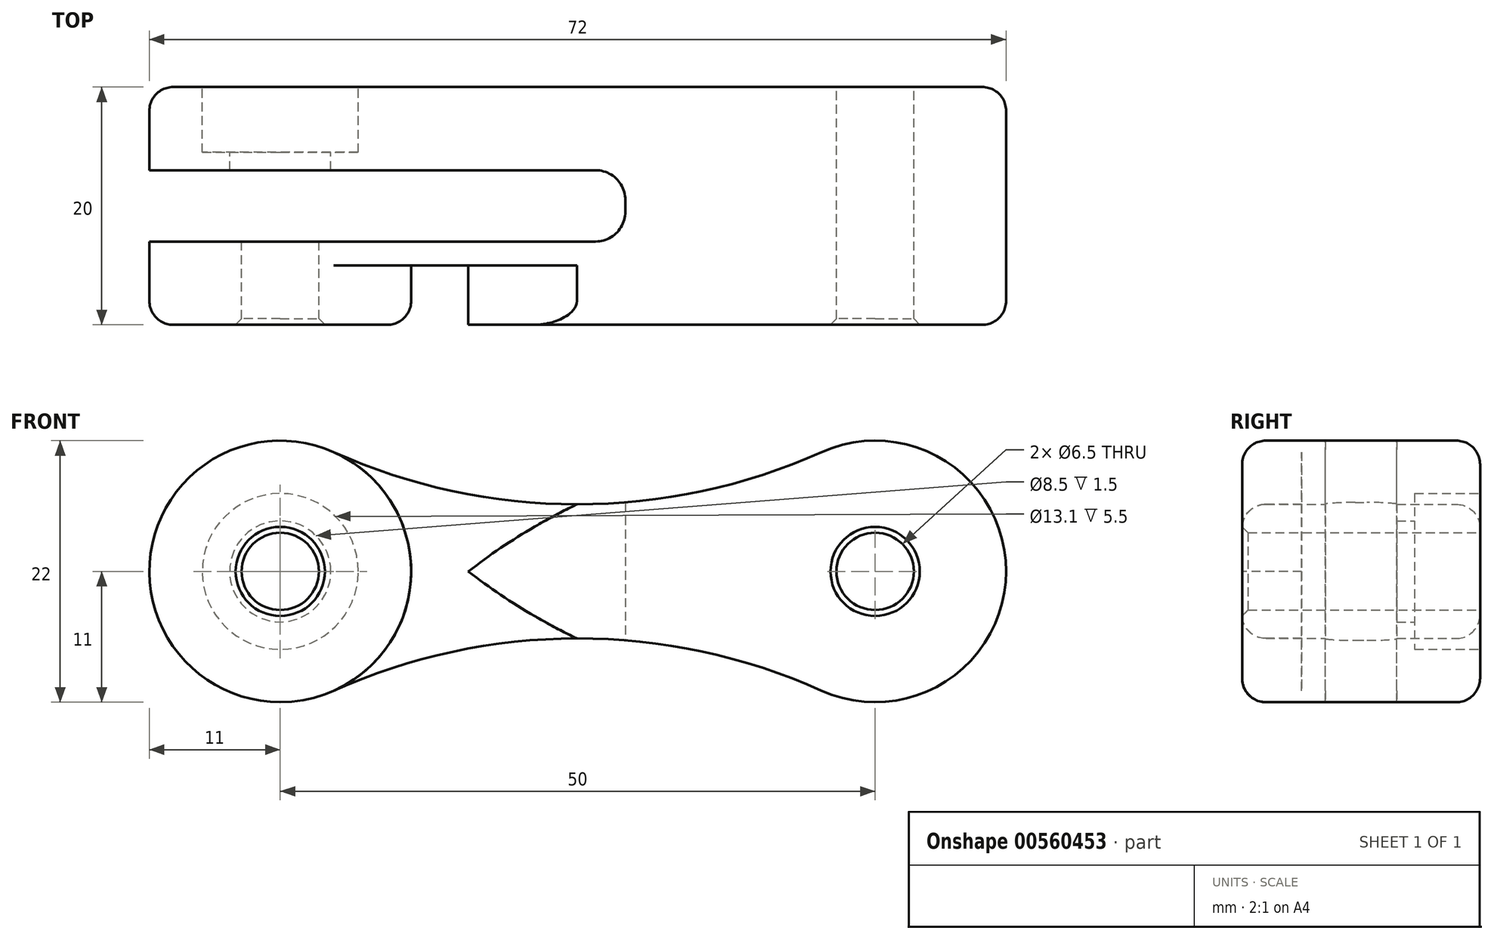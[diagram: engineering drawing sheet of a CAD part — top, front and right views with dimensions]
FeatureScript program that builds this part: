
annotation { "Feature Type Name" : "Feature", "Feature Type Description" : "" }
export const myFeature = defineFeature(function(context is Context, id is Id, definition is map)
    precondition{}
    {
        {
            var Q0;
            Q0=qCreatedBy(makeId("Front.planeOp"),FACE);
            var sketch = newSketch(context, id + "F0", { "sketchPlane" : qUnion([Q0])});
            skArc(sketch, "E0", {"start": v(-20.5, 10.03) * mm, "mid": v(-36, 0) * mm, "end": v(-20.5, -10.03) * mm});
            skArc(sketch, "E1", {"start": v(20.5, -10.03) * mm, "mid": v(36, 0) * mm, "end": v(20.5, 10.03) * mm});
            skArc(sketch, "E2", {"start": v(-20.5, 10.03) * mm, "mid": v(0, 5.64) * mm, "end": v(20.5, 10.03) * mm});
            skLineSegment(sketch, "E3", {"start": v(-25, 0) * mm, "end": v(25, 0) * mm, "construction": true});
            skArc(sketch, "E4.MirrorC", {"start": v(-20.5, -10.03) * mm, "mid": v(0, -5.64) * mm, "end": v(20.5, -10.03) * mm});
            skSolve(sketch);
        }
        {
            var Q0;
            Q0=makeQuery(id+"F0.imprint","IMPRINT",FACE,{"disambiguationData":[TD([[makeQuery(id+"F0.imprint","IMPRINT",EDGE,{"derivedFrom":sQuery(id+"F0.wireOp",EDGE,"E0")}),1.0]])]});
            extrude(context, id + "F1", {"entities" : qUnion([Q0]), "endBound" : BoundingType.SYMMETRIC, "depth" : 20 * mm, "offsetDistance" : 25 * mm});
        }
        {
            var Q0;
            Q0=makeQuery(id+"F1.opExtrude","CAP_FACE",FACE,{"disambiguationData":[OSD([sQuery(id+"F0.wireOp",EDGE,"E0"),sQuery(id+"F0.wireOp",EDGE,"E1"),sQuery(id+"F0.wireOp",EDGE,"E2"),sQuery(id+"F0.wireOp",EDGE,"E4.MirrorC")])],"isStart":true});
            var sketch = newSketch(context, id + "F2", { "sketchPlane" : qUnion([Q0])});
            skCircle(sketch, "E5", {"center": v(25, 0) * mm, "radius": 4.25 * mm});
            skCircle(sketch, "E6", {"center": v(-25, 0) * mm, "radius": 4.25 * mm});
            skSolve(sketch);
        }
        {
            var Q0;
            Q0=makeQuery(id+"F2.imprint","IMPRINT",FACE,{"disambiguationData":[TD([[makeQuery(id+"F2.imprint","IMPRINT",EDGE,{"derivedFrom":sQuery(id+"F2.wireOp",EDGE,"E5")}),-1.0]])]});
            var sketch = newSketch(context, id + "F3", { "sketchPlane" : qUnion([Q0])});
            skCircle(sketch, "E7", {"center": v(-25, 0) * mm, "radius": 3.25 * mm});
            skCircle(sketch, "E8", {"center": v(25, 0) * mm, "radius": 3.25 * mm});
            skSolve(sketch);
        }
        {
            var Q0;
            Q0=makeQuery(id+"F3.imprint","IMPRINT",FACE,{"disambiguationData":[TD([[makeQuery(id+"F3.imprint","IMPRINT",EDGE,{"derivedFrom":sQuery(id+"F3.wireOp",EDGE,"E7")}),1.0]])]});
            var Q1;
            Q1=makeQuery(id+"F3.imprint","IMPRINT",FACE,{"disambiguationData":[TD([[makeQuery(id+"F3.imprint","IMPRINT",EDGE,{"derivedFrom":sQuery(id+"F3.wireOp",EDGE,"E8")}),1.0]])]});
            extrude(context, id + "F4", {"entities" : qUnion([Q0, Q1]), "operationType" : NewBodyOperationType.REMOVE, "endBound" : BoundingType.THROUGH_ALL, "oppositeDirection" : true, "depth" : 25 * mm, "offsetDistance" : 25 * mm});
        }
        {
            var Q0;
            Q0=makeQuery(id+"F2.imprint","IMPRINT",FACE,{"disambiguationData":[TD([[makeQuery(id+"F2.imprint","IMPRINT",EDGE,{"derivedFrom":sQuery(id+"F2.wireOp",EDGE,"E5")}),1.0]])]});
            extrude(context, id + "F5", {"entities" : qUnion([Q0]), "operationType" : NewBodyOperationType.REMOVE, "oppositeDirection" : true, "depth" : 9 * mm, "offsetDistance" : 25 * mm});
        }
        {
            var Q0;
            Q0=makeQuery(id+"F1.opExtrude","CAP_FACE",FACE,{"disambiguationData":[OSD([sQuery(id+"F0.wireOp",EDGE,"E0"),sQuery(id+"F0.wireOp",EDGE,"E1"),sQuery(id+"F0.wireOp",EDGE,"E2"),sQuery(id+"F0.wireOp",EDGE,"E4.MirrorC")])],"isStart":true});
            var sketch = newSketch(context, id + "F6", { "sketchPlane" : qUnion([Q0])});
            skCircle(sketch, "E9", {"center": v(25, 0) * mm, "radius": 6.55 * mm});
            skSolve(sketch);
        }
        {
            var Q0;
            Q0=makeQuery(id+"F6.imprint","IMPRINT",FACE,{"disambiguationData":[TD([[makeQuery(id+"F6.imprint","IMPRINT",EDGE,{"derivedFrom":sQuery(id+"F6.wireOp",EDGE,"E9")}),1.0]])]});
            extrude(context, id + "F7", {"entities" : qUnion([Q0]), "operationType" : NewBodyOperationType.REMOVE, "oppositeDirection" : true, "depth" : 5.5 * mm, "offsetDistance" : 25 * mm});
        }
        {
            var Q0;
            Q0=makeQuery(id+"F1.opExtrude","CAP_FACE",FACE,{"disambiguationData":[OSD([sQuery(id+"F0.wireOp",EDGE,"E0"),sQuery(id+"F0.wireOp",EDGE,"E1"),sQuery(id+"F0.wireOp",EDGE,"E2"),sQuery(id+"F0.wireOp",EDGE,"E4.MirrorC")])],"isStart":false});
            var sketch = newSketch(context, id + "F8", { "sketchPlane" : qUnion([Q0])});
            skArc(sketch, "E10", {"start": v(-9.19, 0) * mm, "mid": v(-2.1, -4.6) * mm, "end": v(5.65, -7.96) * mm});
            skLineSegment(sketch, "E11", {"start": v(-45.02, 0) * mm, "end": v(-102.32, 0) * mm, "construction": true});
            skArc(sketch, "E12.MirrorC", {"start": v(-9.19, 0) * mm, "mid": v(-2.1, 4.6) * mm, "end": v(5.65, 7.96) * mm});
            skLineSegment(sketch, "E13", {"start": v(5.65, -7.96) * mm, "end": v(-41.27, -16.1) * mm});
            skLineSegment(sketch, "E14", {"start": v(-41.27, -16.1) * mm, "end": v(-41.27, 0) * mm});
            skLineSegment(sketch, "E15.MirrorCS", {"start": v(-41.27, 16.1) * mm, "end": v(-41.27, 0) * mm});
            skLineSegment(sketch, "E16.MirrorCS", {"start": v(5.65, 7.96) * mm, "end": v(-41.27, 16.1) * mm});
            skCircle(sketch, "E17", {"center": v(-25, 0) * mm, "radius": 11 * mm});
            skSolve(sketch);
        }
        {
            var Q0;
            Q0 = qSketchRegion(id + "F8", true);
            extrude(context, id + "F9", {"entities" : qUnion([Q0]), "operationType" : NewBodyOperationType.REMOVE, "oppositeDirection" : true, "depth" : 5 * mm, "offsetDistance" : 25 * mm});
        }
        {
            var Q0;
            Q0=makeQuery(id+"F1.opExtrude","CAP_FACE",FACE,{"disambiguationData":[OSD([sQuery(id+"F0.wireOp",EDGE,"E0"),sQuery(id+"F0.wireOp",EDGE,"E1"),sQuery(id+"F0.wireOp",EDGE,"E2"),sQuery(id+"F0.wireOp",EDGE,"E4.MirrorC")])],"isStart":true});
            var sketch = newSketch(context, id + "F10", { "sketchPlane" : qUnion([Q0])});
            skLineSegment(sketch, "E18", {"start": v(-17.42, 0) * mm, "end": v(-74.72, 0) * mm, "construction": true});
            skLineSegment(sketch, "E19", {"start": v(41.27, -16.1) * mm, "end": v(41.27, 0) * mm});
            skLineSegment(sketch, "E20.MirrorCS", {"start": v(41.27, 16.1) * mm, "end": v(41.27, 0) * mm});
            skLineSegment(sketch, "E21.MirrorCS", {"start": v(-5.65, -7.96) * mm, "end": v(41.27, -16.1) * mm});
            skLineSegment(sketch, "E22.MirrorCS", {"start": v(-5.65, 7.96) * mm, "end": v(41.27, 16.1) * mm});
            skArc(sketch, "E23.MirrorCS", {"start": v(9.19, 0) * mm, "mid": v(2.1, -4.6) * mm, "end": v(-5.65, -7.96) * mm});
            skArc(sketch, "E24.MirrorCS", {"start": v(9.19, 0) * mm, "mid": v(2.1, 4.6) * mm, "end": v(-5.65, 7.96) * mm});
            skCircle(sketch, "E25.MirrorC", {"center": v(25, 0) * mm, "radius": 11 * mm});
            skSolve(sketch);
        }
        {
            var Q0;
            Q0=makeQuery(id+"F10.imprint","IMPRINT",FACE,{"disambiguationData":[TD([[makeQuery(id+"F10.imprint","IMPRINT",EDGE,{"derivedFrom":sQuery(id+"F10.wireOp",EDGE,"E19")}),1.0]])]});
            var Q1;
            {var subQ0=sQuery(id+"F10.wireOp",EDGE,"E24.MirrorCS");var subQ1=sQuery(id+"F10.wireOp",EDGE,"E23.MirrorCS");var subQ2=makeQuery(id+"F10.imprint","INTERSECT",VERTEX,{"derivedFrom":[subQ1,subQ0]});Q1=makeQuery(id+"F10.imprint","IMPRINT",FACE,{"disambiguationData":[TD([[makeQuery(id+"F10.imprint","IMPRINT",EDGE,{"disambiguationData":[TD([[subQ2,-1.0]])],"derivedFrom":subQ1}),1.0]])]});}
            extrude(context, id + "F11", {"entities" : qUnion([Q0, Q1]), "operationType" : NewBodyOperationType.REMOVE, "oppositeDirection" : true, "depth" : 5 * mm, "offsetDistance" : 25 * mm});
        }
        {
            var Q0;
            Q0=makeQuery(id+"F9.boolean.opBoolean","MERGE",EDGE,{"derivedFrom":[makeQuery(id+"F1.opExtrude","CAP_EDGE",EDGE,{"disambiguationData":[OSD([sQuery(id+"F0.wireOp",EDGE,"E0")])],"isStart":false}),makeQuery(id+"F9.opExtrude","CAP_EDGE",EDGE,{"disambiguationData":[OSD([sQuery(id+"F8.wireOp",EDGE,"E17")])],"isStart":true})]});
            var Q1;
            Q1=makeQuery(id+"F9.boolean.opBoolean","COPY",EDGE,{"derivedFrom":makeQuery(id+"F9.opExtrude","CAP_EDGE",EDGE,{"disambiguationData":[OSD([sQuery(id+"F8.wireOp",EDGE,"E10")])],"isStart":true})});
            var Q2;
            Q2=makeQuery(id+"F9.boolean.opBoolean","COPY",EDGE,{"derivedFrom":makeQuery(id+"F9.opExtrude","CAP_EDGE",EDGE,{"disambiguationData":[OSD([sQuery(id+"F8.wireOp",EDGE,"E12.MirrorC")])],"isStart":true})});
            var Q3;
            Q3=makeQuery(id+"F1.opExtrude","CAP_EDGE",EDGE,{"disambiguationData":[OSD([sQuery(id+"F0.wireOp",EDGE,"E2")])],"isStart":false});
            var Q4;
            Q4=makeQuery(id+"F1.opExtrude","CAP_EDGE",EDGE,{"disambiguationData":[OSD([sQuery(id+"F0.wireOp",EDGE,"E4.MirrorC")])],"isStart":true});
            var Q5;
            Q5=makeQuery(id+"F11.boolean.opBoolean","COPY",EDGE,{"derivedFrom":makeQuery(id+"F11.opExtrude","CAP_EDGE",EDGE,{"disambiguationData":[OSD([sQuery(id+"F10.wireOp",EDGE,"E23.MirrorCS")])],"isStart":true})});
            var Q6;
            Q6=makeQuery(id+"F11.boolean.opBoolean","COPY",EDGE,{"derivedFrom":makeQuery(id+"F11.opExtrude","CAP_EDGE",EDGE,{"disambiguationData":[OSD([sQuery(id+"F10.wireOp",EDGE,"E24.MirrorCS")])],"isStart":true})});
            var Q7;
            Q7=makeQuery(id+"F11.boolean.opBoolean","MERGE",EDGE,{"derivedFrom":[makeQuery(id+"F1.opExtrude","CAP_EDGE",EDGE,{"disambiguationData":[OSD([sQuery(id+"F0.wireOp",EDGE,"E0")])],"isStart":true}),makeQuery(id+"F11.opExtrude","CAP_EDGE",EDGE,{"disambiguationData":[OSD([sQuery(id+"F10.wireOp",EDGE,"E25.MirrorC")])],"isStart":true})]});
            fillet(context, id + "F12", {"entities" : qUnion([Q0, Q1, Q2, Q3, Q4, Q5, Q6, Q7]), "radius" : 2 * mm, "tangentPropagation" : true, "allowEdgeOverflow" : false});
        }
        {
            var Q0;
            Q0=qCreatedBy(makeId("Right.planeOp"),FACE);
            cPlane(context, id + "F13", {"entities" : qUnion([Q0]), "cplaneType" : CPlaneType.OFFSET, "offset" : 36 * mm, "oppositeDirection" : true, "width" : 150 * mm, "height" : 150 * mm});
        }
        {
            var Q0;
            Q0=qCreatedBy(id+"F13.planeOp",FACE);
            var sketch = newSketch(context, id + "F14", { "sketchPlane" : qUnion([Q0])});
            skLineSegment(sketch, "E26.bottom", {"start": v(-3, 15) * mm, "end": v(3, 15) * mm});
            skLineSegment(sketch, "E26.top", {"start": v(-3, -15) * mm, "end": v(3, -15) * mm});
            skLineSegment(sketch, "E26.left", {"start": v(-3, 15) * mm, "end": v(-3, -15) * mm});
            skLineSegment(sketch, "E26.right", {"start": v(3, 15) * mm, "end": v(3, -15) * mm});
            skPoint(sketch, "E26.middle", {"position": v(0, 0) * mm});
            skSolve(sketch);
        }
        {
            var Q0;
            Q0 = qSketchRegion(id + "F14", true);
            extrude(context, id + "F15", {"entities" : qUnion([Q0]), "operationType" : NewBodyOperationType.REMOVE, "depth" : 40 * mm, "offsetDistance" : 25 * mm});
        }
        {
            var Q0;
            Q0=makeQuery(id+"F15.boolean.opBoolean","COPY",EDGE,{"derivedFrom":makeQuery(id+"F15.opExtrude","CAP_EDGE",EDGE,{"disambiguationData":[OSD([sQuery(id+"F14.wireOp",EDGE,"E26.right")])],"isStart":false})});
            var Q1;
            Q1=makeQuery(id+"F15.boolean.opBoolean","COPY",EDGE,{"derivedFrom":makeQuery(id+"F15.opExtrude","CAP_EDGE",EDGE,{"disambiguationData":[OSD([sQuery(id+"F14.wireOp",EDGE,"E26.left")])],"isStart":false})});
            fillet(context, id + "F16", {"entities" : qUnion([Q0, Q1]), "radius" : 2.5 * mm, "tangentPropagation" : true, "allowEdgeOverflow" : false});
        }
        {
            var Q0;
            Q0=makeQuery(id+"F4.boolean.opBoolean","INTERSECT",EDGE,{"derivedFrom":[makeQuery(id+"F1.opExtrude","CAP_FACE",FACE,{"disambiguationData":[OSD([sQuery(id+"F0.wireOp",EDGE,"E0"),sQuery(id+"F0.wireOp",EDGE,"E1"),sQuery(id+"F0.wireOp",EDGE,"E2"),sQuery(id+"F0.wireOp",EDGE,"E4.MirrorC")])],"isStart":false}),makeQuery(id+"F4.opExtrude","SWEPT_FACE",FACE,{"disambiguationData":[OSD([sQuery(id+"F3.wireOp",EDGE,"E8")])]})]});
            var Q1;
            Q1=makeQuery(id+"F4.boolean.opBoolean","INTERSECT",EDGE,{"derivedFrom":[makeQuery(id+"F1.opExtrude","CAP_FACE",FACE,{"disambiguationData":[OSD([sQuery(id+"F0.wireOp",EDGE,"E0"),sQuery(id+"F0.wireOp",EDGE,"E1"),sQuery(id+"F0.wireOp",EDGE,"E2"),sQuery(id+"F0.wireOp",EDGE,"E4.MirrorC")])],"isStart":false}),makeQuery(id+"F4.opExtrude","SWEPT_FACE",FACE,{"disambiguationData":[OSD([sQuery(id+"F3.wireOp",EDGE,"E7")])]})]});
            var Q2;
            Q2=makeQuery(id+"F4.boolean.opBoolean","COPY",EDGE,{"derivedFrom":makeQuery(id+"F4.opExtrude","CAP_EDGE",EDGE,{"disambiguationData":[OSD([sQuery(id+"F3.wireOp",EDGE,"E7")])],"isStart":true})});
            chamfer(context, id + "F17", {"entities" : qUnion([Q0, Q1, Q2]), "width" : .5 * mm, "tangentPropagation" : true});
        }
    });
